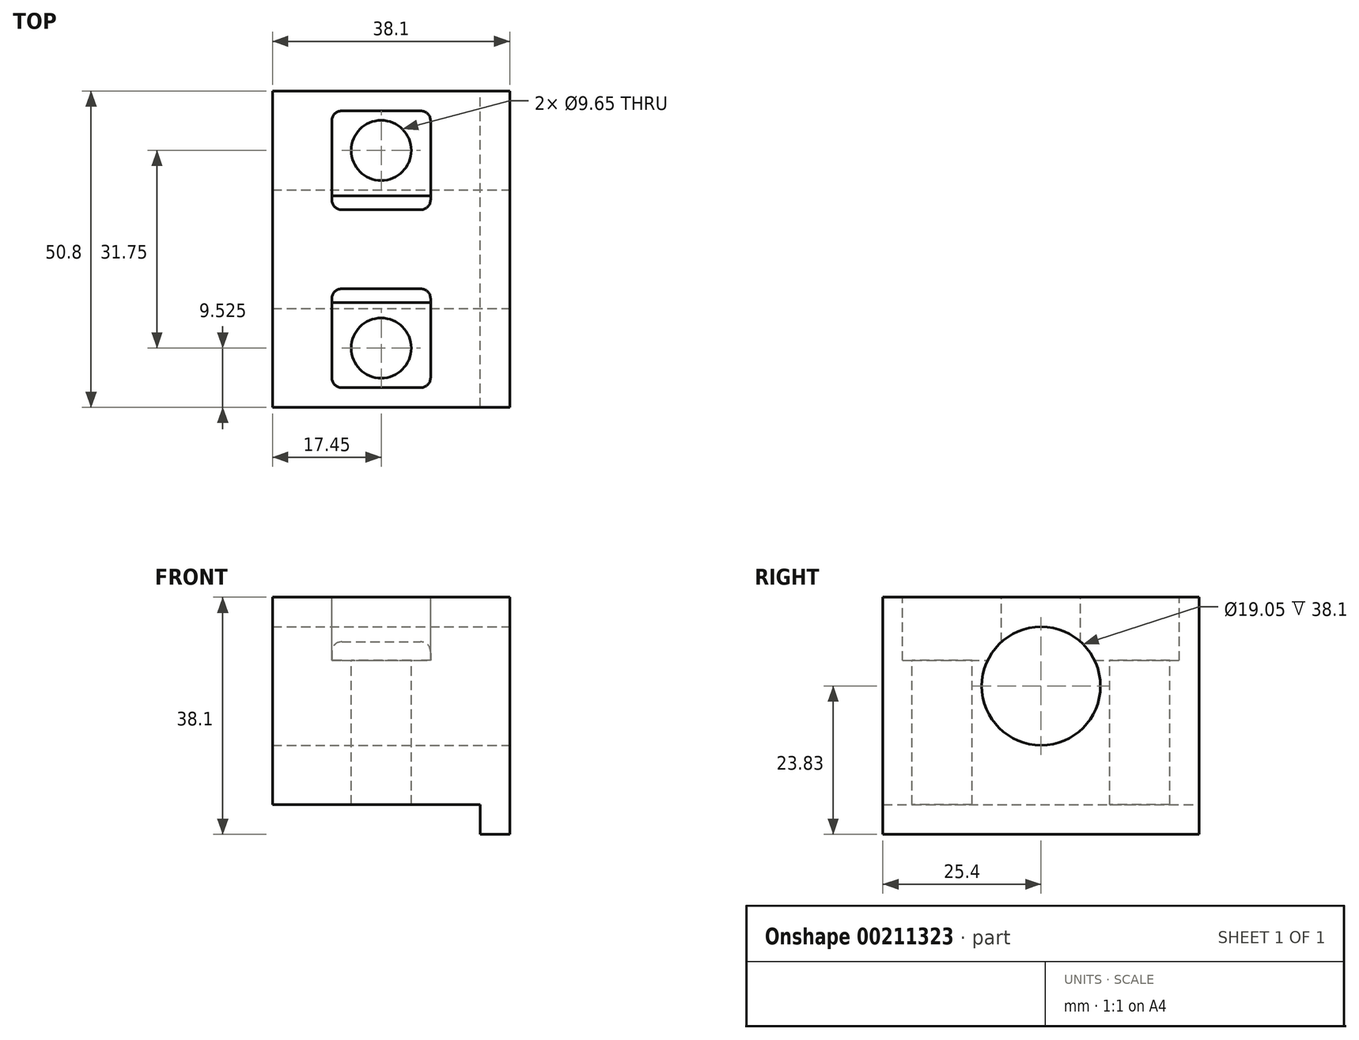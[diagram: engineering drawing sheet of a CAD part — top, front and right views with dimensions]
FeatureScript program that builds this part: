
annotation { "Feature Type Name" : "Feature", "Feature Type Description" : "" }
export const myFeature = defineFeature(function(context is Context, id is Id, definition is map)
    precondition{}
    {
        {
            var Q0;
            Q0=qCreatedBy(makeId("Front.planeOp"),FACE);
            var sketch = newSketch(context, id + "F0", { "sketchPlane" : qUnion([Q0])});
            skLineSegment(sketch, "E0", {"start": v(0, 0) * mm, "end": v(33.32, 0) * mm});
            skLineSegment(sketch, "E1", {"start": v(33.32, 0) * mm, "end": v(33.32, -4.78) * mm});
            skLineSegment(sketch, "E2", {"start": v(33.32, -4.78) * mm, "end": v(38.1, -4.78) * mm});
            skLineSegment(sketch, "E3", {"start": v(38.1, -4.78) * mm, "end": v(38.1, 33.32) * mm});
            skLineSegment(sketch, "E4", {"start": v(38.1, 33.32) * mm, "end": v(0, 33.32) * mm});
            skLineSegment(sketch, "E5", {"start": v(0, 33.32) * mm, "end": v(0, 0) * mm});
            skSolve(sketch);
        }
        {
            var Q0;
            Q0 = qSketchRegion(id + "F0", true);
            extrude(context, id + "F1", {"entities" : qUnion([Q0]), "depth" : 50.8 * mm});
        }
        {
            var Q0;
            Q0=makeQuery(id+"F1.opExtrude","SWEPT_FACE",FACE,{"disambiguationData":[OSD([sQuery(id+"F0.wireOp",EDGE,"E3")])]});
            var sketch = newSketch(context, id + "F2", { "sketchPlane" : qUnion([Q0])});
            skLineSegment(sketch, "E6.bottom", {"start": v(-50.8, 0) * mm, "end": v(0, 0) * mm});
            skLineSegment(sketch, "E6.top", {"start": v(-50.8, 33.32) * mm, "end": v(0, 33.32) * mm});
            skLineSegment(sketch, "E6.left", {"start": v(-50.8, 0) * mm, "end": v(-50.8, 33.32) * mm});
            skLineSegment(sketch, "E6.right", {"start": v(0, 0) * mm, "end": v(0, 33.32) * mm});
            skLineSegment(sketch, "E7", {"start": v(-25.4, 33.32) * mm, "end": v(-25.4, 0) * mm, "construction": true});
            skCircle(sketch, "E8", {"center": v(-25.4, 19.05) * mm, "radius": 9.53 * mm});
            skSolve(sketch);
        }
        {
            var Q0;
            Q0=makeQuery(id+"F1.opExtrude","SWEPT_FACE",FACE,{"disambiguationData":[OSD([sQuery(id+"F0.wireOp",EDGE,"E4")])]});
            var sketch = newSketch(context, id + "F3", { "sketchPlane" : qUnion([Q0])});
            skLineSegment(sketch, "E9", {"start": v(17.45, 0) * mm, "end": v(17.45, -50.8) * mm, "construction": true});
            skCircle(sketch, "E10", {"center": v(17.45, -9.53) * mm, "radius": 4.83 * mm});
            skCircle(sketch, "E11", {"center": v(17.45, -41.28) * mm, "radius": 4.83 * mm});
            skLineSegment(sketch, "E12", {"start": v(0, -25.4) * mm, "end": v(38.1, -25.4) * mm, "construction": true});
            skLineSegment(sketch, "E13.bottom", {"start": v(9.51, -47.63) * mm, "end": v(25.39, -47.63) * mm});
            skLineSegment(sketch, "E13.top", {"start": v(9.51, -31.75) * mm, "end": v(25.39, -31.75) * mm});
            skLineSegment(sketch, "E13.left", {"start": v(9.51, -47.63) * mm, "end": v(9.51, -31.75) * mm});
            skLineSegment(sketch, "E13.right", {"start": v(25.39, -47.62) * mm, "end": v(25.39, -31.75) * mm});
            skLineSegment(sketch, "E14.bottom", {"start": v(9.51, -19.05) * mm, "end": v(25.39, -19.05) * mm});
            skLineSegment(sketch, "E14.top", {"start": v(9.51, -3.18) * mm, "end": v(25.39, -3.18) * mm});
            skLineSegment(sketch, "E14.left", {"start": v(9.51, -19.05) * mm, "end": v(9.51, -3.18) * mm});
            skLineSegment(sketch, "E14.right", {"start": v(25.39, -19.05) * mm, "end": v(25.39, -3.18) * mm});
            skLineSegment(sketch, "E15", {"start": v(17.45, -47.63) * mm, "end": v(17.45, -31.75) * mm, "construction": true});
            skSolve(sketch);
        }
        {
            var Q0;
            Q0=makeQuery(id+"F2.imprint","IMPRINT",FACE,{"disambiguationData":[TD([[makeQuery(id+"F2.imprint","IMPRINT",EDGE,{"derivedFrom":sQuery(id+"F2.wireOp",EDGE,"E8")}),1.0]])]});
            extrude(context, id + "F4", {"entities" : qUnion([Q0]), "operationType" : NewBodyOperationType.REMOVE, "endBound" : BoundingType.THROUGH_ALL, "oppositeDirection" : true, "depth" : 25.4 * mm});
        }
        {
            var Q0;
            Q0=makeQuery(id+"F3.imprint","IMPRINT",FACE,{"disambiguationData":[TD([[makeQuery(id+"F3.imprint","IMPRINT",EDGE,{"derivedFrom":sQuery(id+"F3.wireOp",EDGE,"E10")}),1.0]])]});
            var Q1;
            Q1=makeQuery(id+"F3.imprint","IMPRINT",FACE,{"disambiguationData":[TD([[makeQuery(id+"F3.imprint","IMPRINT",EDGE,{"derivedFrom":sQuery(id+"F3.wireOp",EDGE,"E11")}),1.0]])]});
            extrude(context, id + "F5", {"entities" : qUnion([Q0, Q1]), "operationType" : NewBodyOperationType.REMOVE, "endBound" : BoundingType.THROUGH_ALL, "oppositeDirection" : true, "depth" : 25.4 * mm});
        }
        {
            var Q0;
            Q0=makeQuery(id+"F1.opExtrude","CAP_FACE",FACE,{"disambiguationData":[OSD([sQuery(id+"F0.wireOp",EDGE,"E0"),sQuery(id+"F0.wireOp",EDGE,"E1"),sQuery(id+"F0.wireOp",EDGE,"E2"),sQuery(id+"F0.wireOp",EDGE,"E3"),sQuery(id+"F0.wireOp",EDGE,"E4"),sQuery(id+"F0.wireOp",EDGE,"E5")])],"isStart":false});
            var sketch = newSketch(context, id + "F6", { "sketchPlane" : qUnion([Q0])});
            skPoint(sketch, "E16", {"position": v(6.35, 19.05) * mm});
            skPoint(sketch, "E17", {"position": v(31.75, 19.05) * mm});
            skLineSegment(sketch, "E18", {"start": v(6.35, 19.05) * mm, "end": v(31.75, 19.05) * mm, "construction": true});
            skSolve(sketch);
        }
        {
            var Q0;
            Q0=makeQuery(id+"F6.imprint","IMPRINT",FACE,{"disambiguationData":[TD([[makeQuery(id+"F6.imprint","IMPRINT",EDGE,{"derivedFrom":makeQuery(id+"F1.opExtrude","CAP_EDGE",EDGE,{"disambiguationData":[OSD([sQuery(id+"F0.wireOp",EDGE,"E0")])],"isStart":false})}),1.0]])]});
            var sketch = newSketch(context, id + "F7", { "sketchPlane" : qUnion([Q0])});
            skCircle(sketch, "E19", {"center": v(6.35, 19.05) * mm, "radius": 3.18 * mm});
            skCircle(sketch, "E20", {"center": v(31.75, 19.05) * mm, "radius": 3.18 * mm});
            skSolve(sketch);
        }
        {
            var Q0;
            Q0=makeQuery(id+"F3.imprint","IMPRINT",FACE,{"disambiguationData":[TD([[makeQuery(id+"F3.imprint","IMPRINT",EDGE,{"derivedFrom":sQuery(id+"F3.wireOp",EDGE,"E10")}),-1.0]])]});
            var Q1;
            Q1=makeQuery(id+"F3.imprint","IMPRINT",FACE,{"disambiguationData":[TD([[makeQuery(id+"F3.imprint","IMPRINT",EDGE,{"derivedFrom":sQuery(id+"F3.wireOp",EDGE,"E11")}),-1.0]])]});
            extrude(context, id + "F8", {"entities" : qUnion([Q0, Q1]), "operationType" : NewBodyOperationType.REMOVE, "oppositeDirection" : true, "depth" : 10.16 * mm});
        }
        {
            var Q0;
            Q0=makeQuery(id+"F8.boolean.opBoolean","COPY",EDGE,{"derivedFrom":makeQuery(id+"F8.opExtrude","SWEPT_EDGE",EDGE,{"disambiguationData":[OSD([sQuery(id+"F3.wireOp",EDGE,"E13.bottom"),sQuery(id+"F3.wireOp",EDGE,"E13.left")])]})});
            var Q1;
            Q1=makeQuery(id+"F8.boolean.opBoolean","COPY",EDGE,{"derivedFrom":makeQuery(id+"F8.opExtrude","SWEPT_EDGE",EDGE,{"disambiguationData":[OSD([sQuery(id+"F3.wireOp",EDGE,"E13.top"),sQuery(id+"F3.wireOp",EDGE,"E13.left")])]})});
            var Q2;
            Q2=makeQuery(id+"F8.boolean.opBoolean","COPY",EDGE,{"derivedFrom":makeQuery(id+"F8.opExtrude","SWEPT_EDGE",EDGE,{"disambiguationData":[OSD([sQuery(id+"F3.wireOp",EDGE,"E14.top"),sQuery(id+"F3.wireOp",EDGE,"E14.left")])]})});
            var Q3;
            Q3=makeQuery(id+"F8.boolean.opBoolean","COPY",EDGE,{"derivedFrom":makeQuery(id+"F8.opExtrude","SWEPT_EDGE",EDGE,{"disambiguationData":[OSD([sQuery(id+"F3.wireOp",EDGE,"E14.bottom"),sQuery(id+"F3.wireOp",EDGE,"E14.left")])]})});
            var Q4;
            Q4=makeQuery(id+"F8.boolean.opBoolean","COPY",EDGE,{"derivedFrom":makeQuery(id+"F8.opExtrude","SWEPT_EDGE",EDGE,{"disambiguationData":[OSD([sQuery(id+"F3.wireOp",EDGE,"E14.bottom"),sQuery(id+"F3.wireOp",EDGE,"E14.right")])]})});
            var Q5;
            Q5=makeQuery(id+"F8.boolean.opBoolean","COPY",EDGE,{"derivedFrom":makeQuery(id+"F8.opExtrude","SWEPT_EDGE",EDGE,{"disambiguationData":[OSD([sQuery(id+"F3.wireOp",EDGE,"E13.bottom"),sQuery(id+"F3.wireOp",EDGE,"E13.right")])]})});
            var Q6;
            Q6=makeQuery(id+"F8.boolean.opBoolean","COPY",EDGE,{"derivedFrom":makeQuery(id+"F8.opExtrude","SWEPT_EDGE",EDGE,{"disambiguationData":[OSD([sQuery(id+"F3.wireOp",EDGE,"E13.top"),sQuery(id+"F3.wireOp",EDGE,"E13.right")])]})});
            var Q7;
            Q7=makeQuery(id+"F8.boolean.opBoolean","COPY",EDGE,{"derivedFrom":makeQuery(id+"F8.opExtrude","SWEPT_EDGE",EDGE,{"disambiguationData":[OSD([sQuery(id+"F3.wireOp",EDGE,"E14.top"),sQuery(id+"F3.wireOp",EDGE,"E14.right")])]})});
            fillet(context, id + "F9", {"entities" : qUnion([Q0, Q1, Q2, Q3, Q4, Q5, Q6, Q7]), "radius" : 1.6 * mm, "tangentPropagation" : true, "allowEdgeOverflow" : false});
        }
    });
